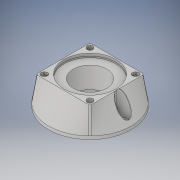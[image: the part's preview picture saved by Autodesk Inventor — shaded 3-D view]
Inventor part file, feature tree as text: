
AUTODESK INVENTOR PART (.ipt)
format: ipt  version: 2017 SP1 (Build 210196100, 196)  size: 739,328 bytes
history: native  units: in
note: dims shown in document units (in); Inventor stores cm internally (conversion verified against a paired STEP export)
features: fillet x1
ambient origin geometry x8: Origin, YZ Plane, XZ Plane, XY Plane, X Axis, Y Axis, Z Axis, Center Point
bodies: Solid1 (feature_tree)
feature tree (1):
  fillet  "Fillet3"  [1 undecoded]
note: 1 required parameter value undecoded (feature->parameter linkage not recoverable at this tier; creation-order binding heuristic only, values carry confidence <= 0.55)
